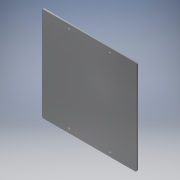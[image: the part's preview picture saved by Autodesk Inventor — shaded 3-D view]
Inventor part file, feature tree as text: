
AUTODESK INVENTOR PART (.ipt)
format: ipt  version: 2017 (Build 210142000, 142)  size: 113,152 bytes
history: native  units: mm
features: sketch x2, extrude x1, hole x1, fillet x1
ambient origin geometry x8: Origin, YZ Plane, XZ Plane, XY Plane, X Axis, Y Axis, Z Axis, Center Point
bodies: Solid1 (feature_tree)
feature tree (5):
  extrude  "Extrusion1"  Depth=3.0mm TaperAngle=0.0deg
  hole  "Hole1"  [1 undecoded]
  fillet  "Fillet1"  Radius=3.0mm
  sketch  "Sketch1"  dims[d0=210.0mm d1=3.0mm d2=0.0mm]
  sketch  "Sketch2"  dims[d3=190.0mm d4=90.5mm d5=3.5mm d6=6.0mm d7=7.0mm d8=2.0mm d9=90.0deg d10=8.0mm d11=20.594885mm d12=3.0mm]
note: 1 required parameter value undecoded (feature->parameter linkage not recoverable at this tier; creation-order binding heuristic only, values carry confidence <= 0.55)
